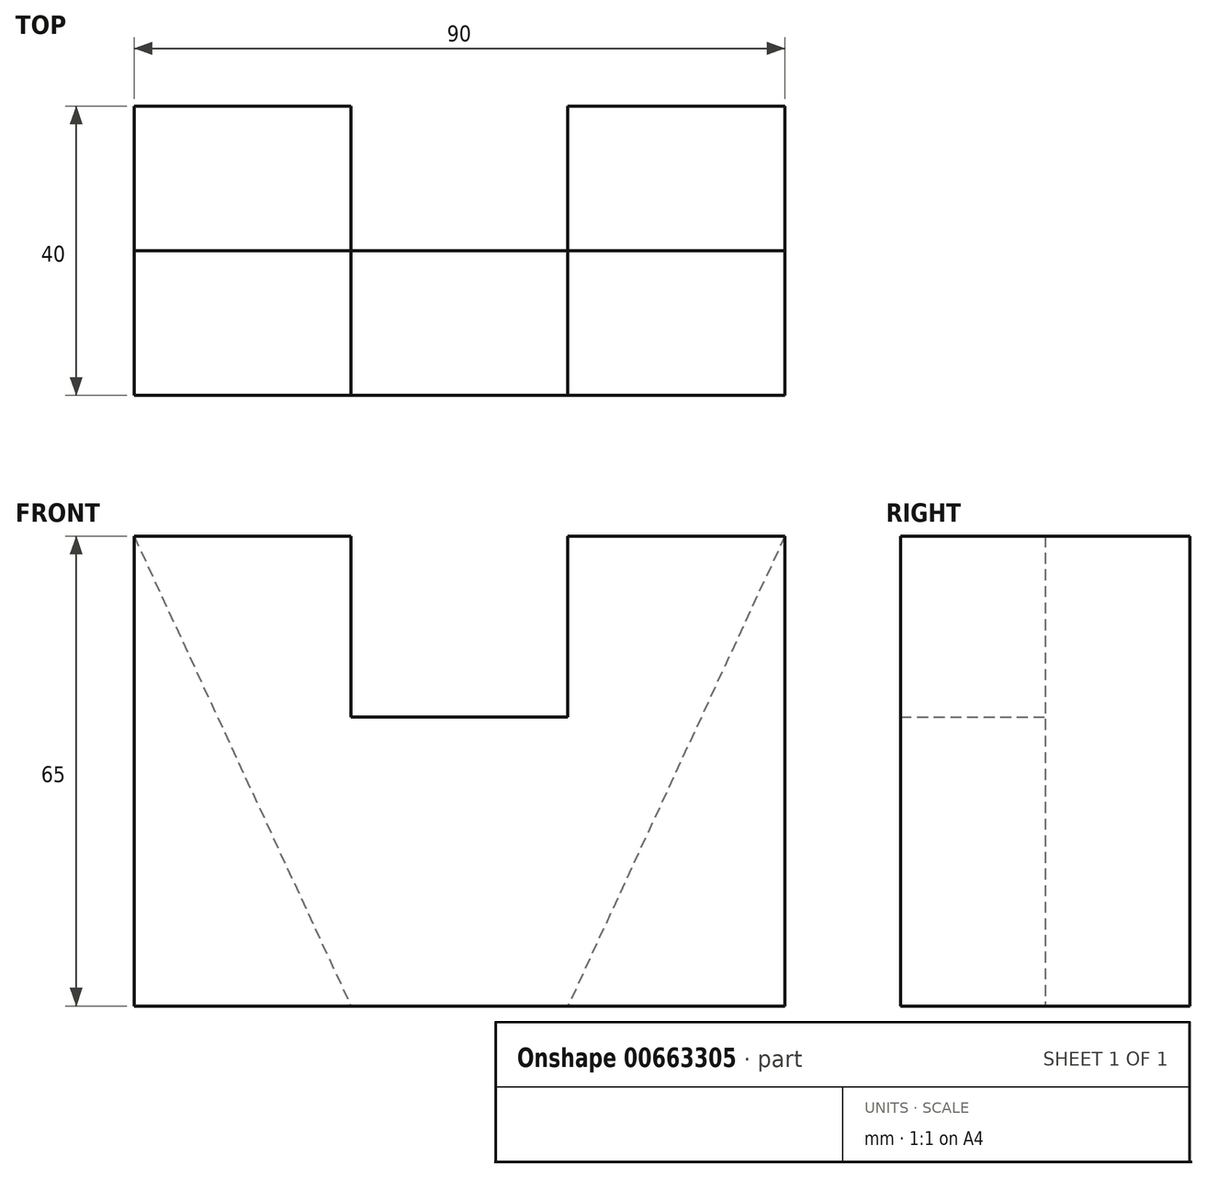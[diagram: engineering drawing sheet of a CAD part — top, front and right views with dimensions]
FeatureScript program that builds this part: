
annotation { "Feature Type Name" : "Feature", "Feature Type Description" : "" }
export const myFeature = defineFeature(function(context is Context, id is Id, definition is map)
    precondition{}
    {
        {
            var Q0;
            Q0=qCreatedBy(makeId("Front.planeOp"),FACE);
            var sketch = newSketch(context, id + "F0", { "sketchPlane" : qUnion([Q0])});
            skLineSegment(sketch, "E0.bottom", {"start": v(-45, 32.5) * mm, "end": v(-15, 32.5) * mm});
            skLineSegment(sketch, "E0.top", {"start": v(-45, -32.5) * mm, "end": v(45, -32.5) * mm});
            skLineSegment(sketch, "E0.left", {"start": v(-45, 32.5) * mm, "end": v(-45, -32.5) * mm});
            skLineSegment(sketch, "E0.right", {"start": v(45, 32.5) * mm, "end": v(45, -32.5) * mm});
            skPoint(sketch, "E0.middle", {"position": v(0, 0) * mm});
            skLineSegment(sketch, "E1", {"start": v(-15, 32.5) * mm, "end": v(-15, 7.5) * mm});
            skLineSegment(sketch, "E2", {"start": v(-15, 7.5) * mm, "end": v(15, 7.5) * mm});
            skLineSegment(sketch, "E3", {"start": v(15, 7.5) * mm, "end": v(15, 32.5) * mm});
            skLineSegment(sketch, "E4", {"start": v(15, 32.5) * mm, "end": v(45, 32.5) * mm});
            skLineSegment(sketch, "E5", {"start": v(-45, 32.5) * mm, "end": v(-15, -32.5) * mm});
            skLineSegment(sketch, "E6", {"start": v(-15, -32.5) * mm, "end": v(-45, -32.5) * mm});
            skLineSegment(sketch, "E7", {"start": v(45, 32.5) * mm, "end": v(15, -32.5) * mm});
            skLineSegment(sketch, "E8", {"start": v(15, -32.5) * mm, "end": v(45, -32.5) * mm});
            skSolve(sketch);
        }
        {
            var Q0;
            Q0 = qSketchRegion(id + "F0", true);
            var Q1;
            Q1 = qSketchRegion(id + "F2", true);
            extrude(context, id + "F1", {"entities" : qUnion([Q0, Q1]), "depth" : 20 * mm, "offsetDistance" : 25 * mm});
        }
        {
            var Q0;
            Q0=qCreatedBy(makeId("Front.planeOp"),FACE);
            var sketch = newSketch(context, id + "F2", { "sketchPlane" : qUnion([Q0])});
            skSolve(sketch);
        }
        {
            var Q0;
            Q0=makeQuery(id+"F0.imprint","IMPRINT",FACE,{"disambiguationData":[TD([[makeQuery(id+"F0.imprint","IMPRINT",EDGE,{"derivedFrom":sQuery(id+"F0.wireOp",EDGE,"E0.left")}),1.0]])]});
            var Q1;
            Q1=makeQuery(id+"F0.imprint","IMPRINT",FACE,{"disambiguationData":[TD([[makeQuery(id+"F0.imprint","IMPRINT",EDGE,{"derivedFrom":sQuery(id+"F0.wireOp",EDGE,"E0.right")}),-1.0]])]});
            extrude(context, id + "F3", {"entities" : qUnion([Q0, Q1]), "operationType" : NewBodyOperationType.ADD, "oppositeDirection" : true, "depth" : 20 * mm, "offsetDistance" : 25 * mm});
        }
    });
